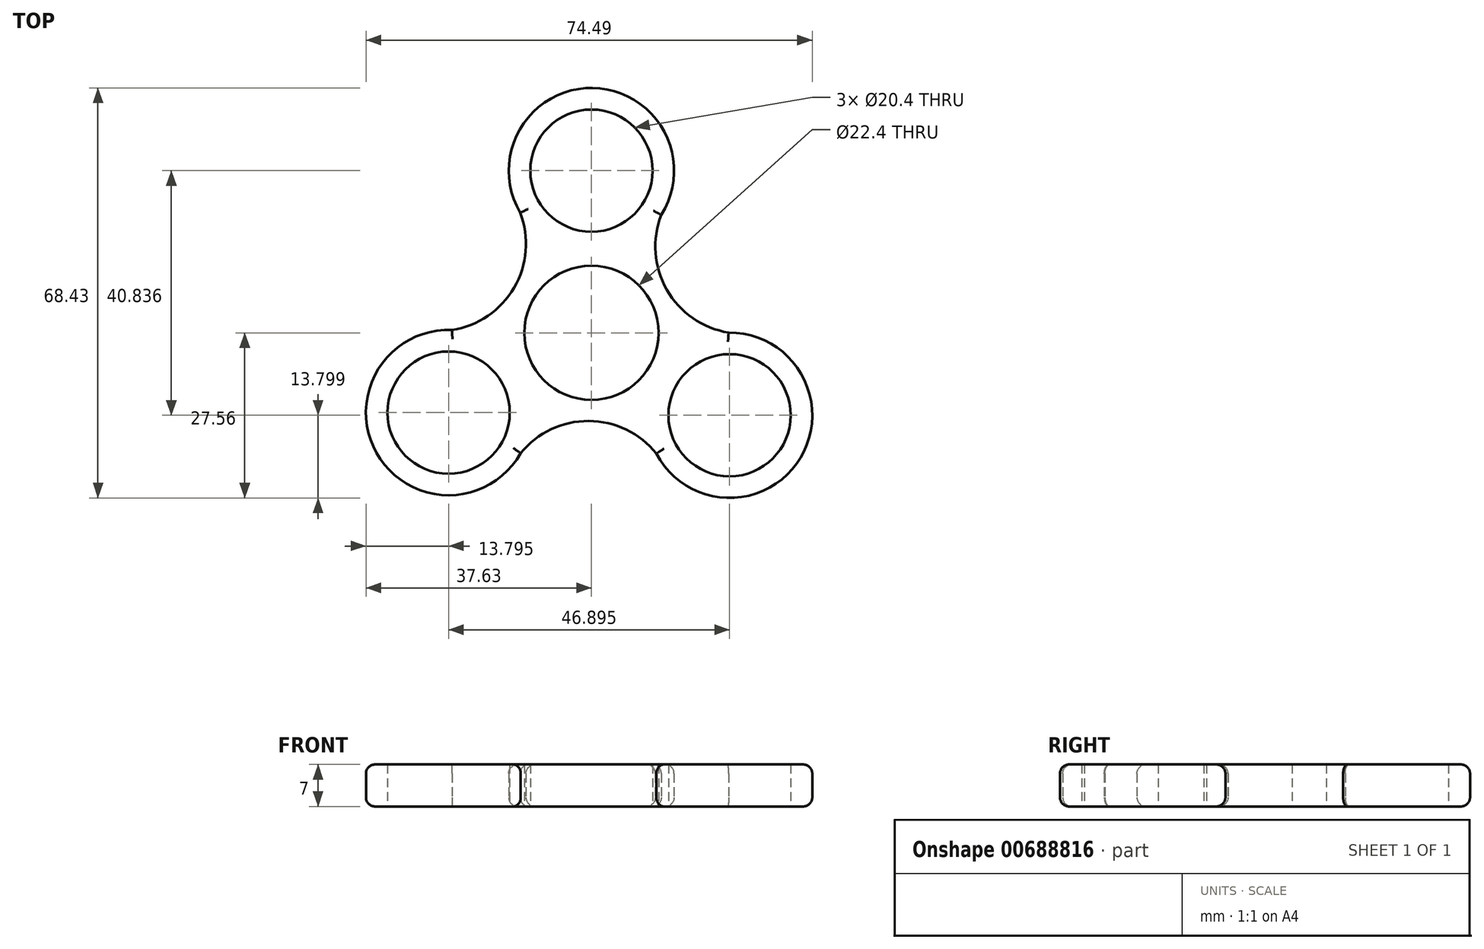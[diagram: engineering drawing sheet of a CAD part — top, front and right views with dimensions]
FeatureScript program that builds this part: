
annotation { "Feature Type Name" : "Feature", "Feature Type Description" : "" }
export const myFeature = defineFeature(function(context is Context, id is Id, definition is map)
    precondition{}
    {
        {
            var Q0;
            Q0=qCreatedBy(makeId("Top.planeOp"),FACE);
            var sketch = newSketch(context, id + "F0", { "sketchPlane" : qUnion([Q0])});
            skCircle(sketch, "E0", {"center": v(0, 0) * mm, "radius": 11.2 * mm});
            skCircle(sketch, "E1", {"center": v(0, 27.07) * mm, "radius": 10.2 * mm});
            skArc(sketch, "E2", {"start": v(11.66, 19.7) * mm, "mid": v(0.2, 40.87) * mm, "end": v(-11.87, 20.04) * mm});
            skArc(sketch, "E3.1.0", {"start": v(-23.27, 0.47) * mm, "mid": v(-35.89, -20.04) * mm, "end": v(-11.8, -20.08) * mm});
            skCircle(sketch, "E3.1.1", {"center": v(-23.83, -13.31) * mm, "radius": 10.2 * mm});
            skArc(sketch, "E3.2.0", {"start": v(10.84, -20.17) * mm, "mid": v(34.9, -20.84) * mm, "end": v(22.9, 0.04) * mm});
            skCircle(sketch, "E3.2.1", {"center": v(23.06, -13.76) * mm, "radius": 10.2 * mm});
            skPoint(sketch, "E3.center", {"position": v(-0.26, 0) * mm});
            skArc(sketch, "E4", {"start": v(12.88, 22.13) * mm, "mid": v(11.97, 8.4) * mm, "end": v(22.9, 0.04) * mm});
            skArc(sketch, "E5.1.0", {"start": v(-26, 0.32) * mm, "mid": v(-13.64, 6.39) * mm, "end": v(-11.87, 20.04) * mm});
            skArc(sketch, "E5.2.0", {"start": v(12.34, -22.45) * mm, "mid": v(0.9, -14.79) * mm, "end": v(-11.8, -20.08) * mm});
            skSolve(sketch);
        }
        {
            var Q0;
            Q0 = qSketchRegion(id + "F0", true);
            extrude(context, id + "F1", {"entities" : qUnion([Q0]), "depth" : 7 * mm, "offsetDistance" : 25 * mm});
        }
        {
            var Q0;
            Q0=makeQuery(id+"F1.opExtrude","CAP_EDGE",EDGE,{"disambiguationData":[OSD([sQuery(id+"F0.wireOp",EDGE,"E2")])],"isStart":false});
            var Q1;
            Q1=makeQuery(id+"F1.opExtrude","CAP_EDGE",EDGE,{"disambiguationData":[OSD([sQuery(id+"F0.wireOp",EDGE,"E5.1.0")])],"isStart":false});
            var Q2;
            Q2=makeQuery(id+"F1.opExtrude","CAP_EDGE",EDGE,{"disambiguationData":[OSD([sQuery(id+"F0.wireOp",EDGE,"E3.1.0")])],"isStart":false});
            var Q3;
            Q3=makeQuery(id+"F1.opExtrude","CAP_EDGE",EDGE,{"disambiguationData":[OSD([sQuery(id+"F0.wireOp",EDGE,"E5.2.0")])],"isStart":false});
            var Q4;
            Q4=makeQuery(id+"F1.opExtrude","CAP_EDGE",EDGE,{"disambiguationData":[OSD([sQuery(id+"F0.wireOp",EDGE,"E3.2.0")])],"isStart":false});
            var Q5;
            Q5=makeQuery(id+"F1.opExtrude","CAP_EDGE",EDGE,{"disambiguationData":[OSD([sQuery(id+"F0.wireOp",EDGE,"E4")])],"isStart":false});
            var Q6;
            Q6=makeQuery(id+"F1.opExtrude","CAP_EDGE",EDGE,{"disambiguationData":[OSD([sQuery(id+"F0.wireOp",EDGE,"E2")])],"isStart":true});
            var Q7;
            Q7=makeQuery(id+"F1.opExtrude","CAP_EDGE",EDGE,{"disambiguationData":[OSD([sQuery(id+"F0.wireOp",EDGE,"E5.1.0")])],"isStart":true});
            var Q8;
            Q8=makeQuery(id+"F1.opExtrude","CAP_EDGE",EDGE,{"disambiguationData":[OSD([sQuery(id+"F0.wireOp",EDGE,"E3.1.0")])],"isStart":true});
            var Q9;
            Q9=makeQuery(id+"F1.opExtrude","CAP_EDGE",EDGE,{"disambiguationData":[OSD([sQuery(id+"F0.wireOp",EDGE,"E5.2.0")])],"isStart":true});
            var Q10;
            Q10=makeQuery(id+"F1.opExtrude","CAP_EDGE",EDGE,{"disambiguationData":[OSD([sQuery(id+"F0.wireOp",EDGE,"E3.2.0")])],"isStart":true});
            var Q11;
            Q11=makeQuery(id+"F1.opExtrude","CAP_EDGE",EDGE,{"disambiguationData":[OSD([sQuery(id+"F0.wireOp",EDGE,"E4")])],"isStart":true});
            fillet(context, id + "F2", {"entities" : qUnion([Q0, Q1, Q2, Q3, Q4, Q5, Q6, Q7, Q8, Q9, Q10, Q11]), "radius" : 1.5 * mm, "tangentPropagation" : true, "allowEdgeOverflow" : false});
        }
    });
